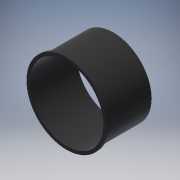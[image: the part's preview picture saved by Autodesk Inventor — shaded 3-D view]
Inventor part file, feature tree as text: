
AUTODESK INVENTOR PART (.ipt)
format: ipt  version: 2016 (Build 200138000, 138)  size: 228,352 bytes
history: native  units: mm
features: extrude x8, sketch x8, fillet x1
ambient origin geometry x8: Origin, YZ Plane, XZ Plane, XY Plane, X Axis, Y Axis, Z Axis, Center Point
bodies: Body1 (feature_tree)
feature tree (17):
  extrude  "Extrusion4"  Depth=36.0mm TaperAngle=0.0deg
  extrude  "Extrusion6"  TaperAngle=0.0deg  [1 undecoded]
  extrude  "Extrusion7"  Depth=36.0mm
  extrude  "Extrusion5"  Depth=2.0mm
  extrude  "Extrusion8"  Depth=2.0mm
  extrude  "Extrusion9"  Depth=2.25mm
  fillet  "Fillet1"  Radius=2.25mm
  extrude  "Extrusion10"  Depth=4.3mm
  extrude  "Extrusion11"  Depth=8.0mm TaperAngle=0.0deg
  sketch  "Sketch4"  dims[d11=58.5mm d12=36.0mm d13=0.0mm]
  sketch  "Sketch5"  dims[d16=0.0mm d17=0.0mm]
  sketch  "Sketch6"  dims[d18=36.0mm d19=0.0mm d20=61.5mm]
  sketch  "Sketch7"  dims[d21=2.0mm d22=0.0mm d23=61.5mm]
  sketch  "Sketch8"  dims[d24=2.0mm d25=0.0mm d26=56.0mm]
  sketch  "Sketch9"  dims[d27=17.0mm d29=2.25mm d30=2.25mm]
  sketch  "Sketch10"  dims[d31=4.3mm d32=4.3mm]
  sketch  "Sketch11"  dims[d33=50.0mm d35=360.0deg d37=8.0mm d38=0.0mm d39=12.5mm d40=2.5mm d41=0.0mm d42=3.0mm d43=4.0mm d44=50.0mm d45=0.0mm d46=2.0mm d47=0.0mm d48=0.0mm d49=0.0mm d50=5.0mm d51=0.0mm]
note: 1 required parameter value undecoded (feature->parameter linkage not recoverable at this tier; creation-order binding heuristic only, values carry confidence <= 0.55)
